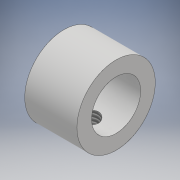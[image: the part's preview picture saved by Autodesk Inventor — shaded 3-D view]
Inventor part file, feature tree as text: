
AUTODESK INVENTOR PART (.ipt)
format: ipt  version: 2017 (Build 210142000, 142)  size: 126,464 bytes
history: native  units: mm
features: sketch x3, extrude x2, fillet x2, hole x1
ambient origin geometry x8: Origin, YZ Plane, XZ Plane, XY Plane, X Axis, Y Axis, Z Axis, Center Point
bodies: Solid1 (feature_tree)
feature tree (8):
  extrude  "Extrusion1"  Depth=15.0mm
  hole  "Hole1"  [1 undecoded]
  extrude  "Extrusion2"  Depth=10.0mm TaperAngle=0.0deg
  fillet  "Fillet1"  Radius=7.5mm
  fillet  "Fillet2"  Radius=7.5mm
  sketch  "Sketch1"  dims[d0=15.0mm d1=15.0mm]
  sketch  "Sketch2"  dims[d2=10.0mm d3=0.0mm]
  sketch  "Sketch3"  dims[d4=3.242mm d5=8.0mm d6=4.0mm d7=2.0mm d8=90.0deg d9=9.8mm d10=20.594885mm d11=9.4mm d12=10.0mm d13=0.0mm d14=7.5mm d15=7.5mm]
note: 1 required parameter value undecoded (feature->parameter linkage not recoverable at this tier; creation-order binding heuristic only, values carry confidence <= 0.55)
